# Revit family: 1Access-Door_Best-Access-Doors_Fiberglass-Reinforced-Gypsum-BA-FGRC-RC
name_source: partatom
category: Specialty Equipment
units: mm (PartAtom-declared; Revit-internal decimal feet)

## family parameters
Cut with Voids When Loaded = No
Host = Face
OmniClass Number = 23.30.10.27.17
Part Type = Normal
Room Calculation Point = No
Round Connector Dimension = Use Diameter
Shared = No

## types (6) — shared parameters
Assembly Code = C1020700
Default Elevation = 0"
Description = Glass Fiber Reinforced Gypsum - Access Door
Frame Depth = 29/32"
Frame Finish = Metal - Best Access Doors - Aluminum
Manufacturer = Best Access Doors
Product Page URL = https://www.bestaccessdoors.com
Product data url = https://bimobject.com
URL = https://www.bestaccessdoors.com

## per-type parameters (varying)
| type | Constraints | Finish | Model |
| 9" x 9" | 1 | Metal - Best Access Doors - Powder Coated White | BA-FGRC-RC-9-9 |
| 12" x 12" | 2 | Metal - Best Access Doors - Powder Coated White | BA-FGRC-RC-12-12 |
| 16" x 16" | 3 | Metal - Best Access Doors - Powder Coated White | BA-FGRC-RC-16-16 |
| 18" x 18" | 4 | Metal - Best Access Doors - Aluminum | BA-FGRC-RC-18-18 |
| 24" x 24" | 5 | Metal - Best Access Doors - Powder Coated White | BA-FGRC-RC-24-24 |
| Custom Size | 6 | Metal - Best Access Doors - Powder Coated White |  |

## geometry (parser evidence)
native form markers: Sweep x3
no freeform markers — native parametric forms only
